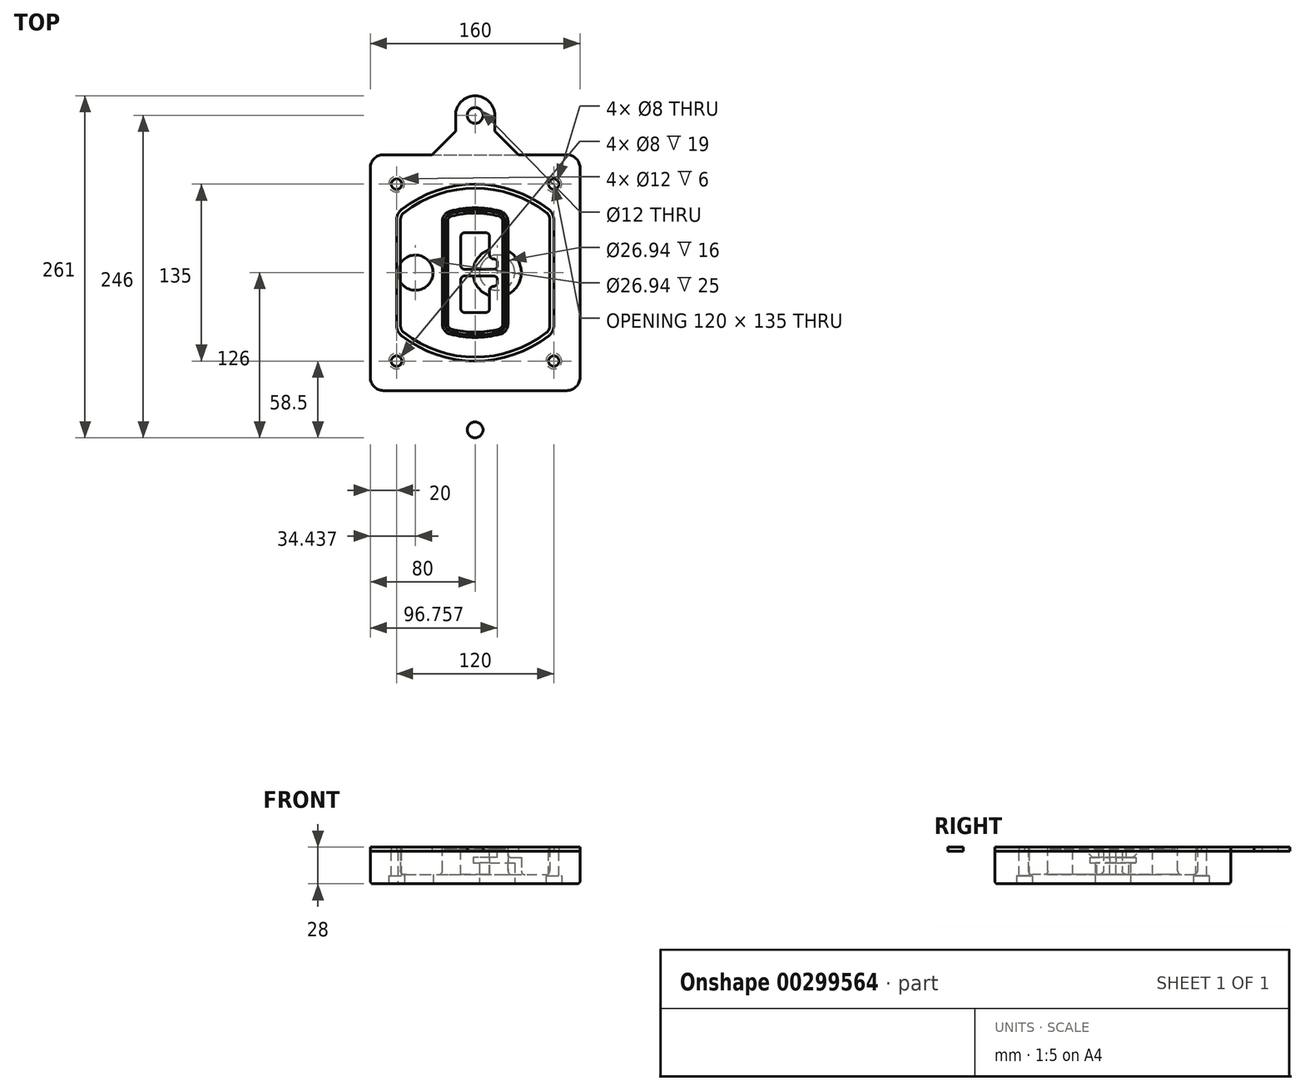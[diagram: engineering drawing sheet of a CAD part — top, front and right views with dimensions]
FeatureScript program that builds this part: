
annotation { "Feature Type Name" : "Feature", "Feature Type Description" : "" }
export const myFeature = defineFeature(function(context is Context, id is Id, definition is map)
    precondition{}
    {
        {
            var Q0;
            Q0=qCreatedBy(makeId("Top.planeOp"),FACE);
            var sketch = newSketch(context, id + "F0", { "sketchPlane" : qUnion([Q0])});
            skPoint(sketch, "E0.rect.middle", {"position": v(0, 0) * mm});
            skLineSegment(sketch, "E1.bottom", {"start": v(-70, -90) * mm, "end": v(70, -90) * mm});
            skLineSegment(sketch, "E1.top", {"start": v(-70, 90) * mm, "end": v(70, 90) * mm});
            skLineSegment(sketch, "E1.left", {"start": v(-80, -80) * mm, "end": v(-80, 80) * mm});
            skLineSegment(sketch, "E1.right", {"start": v(80, -80) * mm, "end": v(80, 80) * mm});
            skLineSegment(sketch, "E2", {"start": v(-80, 90) * mm, "end": v(80, -90) * mm, "construction": true});
            skLineSegment(sketch, "E3", {"start": v(80, 90) * mm, "end": v(-80, -90) * mm, "construction": true});
            skCircle(sketch, "E4", {"center": v(-60, 67.5) * mm, "radius": 4 * mm});
            skCircle(sketch, "E5", {"center": v(60, 67.5) * mm, "radius": 4 * mm});
            skCircle(sketch, "E6", {"center": v(60, -67.5) * mm, "radius": 4 * mm});
            skCircle(sketch, "E7", {"center": v(-60, -67.5) * mm, "radius": 4 * mm});
            skLineSegment(sketch, "E8", {"start": v(-60, 67.5) * mm, "end": v(60, 67.5) * mm, "construction": true});
            skLineSegment(sketch, "E9", {"start": v(60, 67.5) * mm, "end": v(60, -67.5) * mm, "construction": true});
            skLineSegment(sketch, "E10", {"start": v(60, -67.5) * mm, "end": v(-60, -67.5) * mm, "construction": true});
            skLineSegment(sketch, "E11", {"start": v(-60, -67.5) * mm, "end": v(-60, 67.5) * mm, "construction": true});
            skLineSegment(sketch, "E12", {"start": v(-60, 40.3) * mm, "end": v(-60, -40.3) * mm});
            skLineSegment(sketch, "E13", {"start": v(60, 40.3) * mm, "end": v(60, -40.3) * mm});
            skArc(sketch, "E14", {"start": v(56.15, 48.18) * mm, "mid": v(0, 67.5) * mm, "end": v(-56.15, 48.18) * mm});
            skArc(sketch, "E15", {"start": v(-56.15, -48.18) * mm, "mid": v(0, -67.5) * mm, "end": v(56.15, -48.18) * mm});
            skLineSegment(sketch, "E16", {"start": v(-60, 0) * mm, "end": v(60, 0) * mm, "construction": true});
            skPoint(sketch, "E17.visualSharp", {"position": v(-60, -45) * mm});
            skArc(sketch, "E17.filletArc", {"start": v(-60, -40.3) * mm, "mid": v(-58.99, -44.68) * mm, "end": v(-56.15, -48.18) * mm});
            skPoint(sketch, "E18.visualSharp", {"position": v(-60, 45) * mm});
            skArc(sketch, "E18.filletArc", {"start": v(-56.15, 48.18) * mm, "mid": v(-58.99, 44.68) * mm, "end": v(-60, 40.3) * mm});
            skPoint(sketch, "E19.visualSharp", {"position": v(60, 45) * mm});
            skArc(sketch, "E19.filletArc", {"start": v(60, 40.3) * mm, "mid": v(58.99, 44.68) * mm, "end": v(56.15, 48.18) * mm});
            skPoint(sketch, "E20.visualSharp", {"position": v(60, -45) * mm});
            skArc(sketch, "E20.filletArc", {"start": v(56.15, -48.18) * mm, "mid": v(58.99, -44.68) * mm, "end": v(60, -40.3) * mm});
            skPoint(sketch, "E21.visualSharp", {"position": v(-80, 90) * mm});
            skArc(sketch, "E21.filletArc", {"start": v(-70, 90) * mm, "mid": v(-77.07, 87.07) * mm, "end": v(-80, 80) * mm});
            skPoint(sketch, "E22.visualSharp", {"position": v(80, 90) * mm});
            skArc(sketch, "E22.filletArc", {"start": v(80, 80) * mm, "mid": v(77.07, 87.07) * mm, "end": v(70, 90) * mm});
            skPoint(sketch, "E23.visualSharp", {"position": v(80, -90) * mm});
            skArc(sketch, "E23.filletArc", {"start": v(70, -90) * mm, "mid": v(77.07, -87.07) * mm, "end": v(80, -80) * mm});
            skPoint(sketch, "E24.visualSharp", {"position": v(-80, -90) * mm});
            skArc(sketch, "E24.filletArc", {"start": v(-80, -80) * mm, "mid": v(-77.07, -87.07) * mm, "end": v(-70, -90) * mm});
            skArc(sketch, "E25.0", {"start": v(57, 40.3) * mm, "mid": v(56.3, 43.36) * mm, "end": v(54.3, 45.81) * mm});
            skLineSegment(sketch, "E25.1", {"start": v(57, 40.3) * mm, "end": v(57, -40.3) * mm});
            skArc(sketch, "E25.2", {"start": v(54.3, -45.81) * mm, "mid": v(56.3, -43.36) * mm, "end": v(57, -40.3) * mm});
            skArc(sketch, "E25.3", {"start": v(-54.3, -45.81) * mm, "mid": v(0, -64.5) * mm, "end": v(54.3, -45.81) * mm});
            skArc(sketch, "E25.4", {"start": v(-57, -40.3) * mm, "mid": v(-56.3, -43.36) * mm, "end": v(-54.3, -45.81) * mm});
            skArc(sketch, "E25.5", {"start": v(54.3, 45.81) * mm, "mid": v(0, 64.5) * mm, "end": v(-54.3, 45.81) * mm});
            skLineSegment(sketch, "E25.6", {"start": v(-57, 40.3) * mm, "end": v(-57, -40.3) * mm});
            skArc(sketch, "E25.7", {"start": v(-54.3, 45.81) * mm, "mid": v(-56.3, 43.36) * mm, "end": v(-57, 40.3) * mm});
            skArc(sketch, "E26.0", {"start": v(-58.62, 51.33) * mm, "mid": v(-62.58, 46.43) * mm, "end": v(-64, 40.3) * mm});
            skArc(sketch, "E26.1", {"start": v(58.62, 51.33) * mm, "mid": v(0, 71.5) * mm, "end": v(-58.62, 51.33) * mm});
            skArc(sketch, "E26.2", {"start": v(64, 40.3) * mm, "mid": v(62.58, 46.43) * mm, "end": v(58.62, 51.33) * mm});
            skLineSegment(sketch, "E26.3", {"start": v(64, 40.3) * mm, "end": v(64, -40.3) * mm});
            skArc(sketch, "E26.4", {"start": v(58.62, -51.33) * mm, "mid": v(62.58, -46.43) * mm, "end": v(64, -40.3) * mm});
            skLineSegment(sketch, "E26.5", {"start": v(-64, 40.3) * mm, "end": v(-64, -40.3) * mm});
            skArc(sketch, "E26.6", {"start": v(-58.62, -51.33) * mm, "mid": v(0, -71.5) * mm, "end": v(58.62, -51.33) * mm});
            skArc(sketch, "E26.7", {"start": v(-64, -40.3) * mm, "mid": v(-62.58, -46.43) * mm, "end": v(-58.62, -51.33) * mm});
            skSolve(sketch);
        }
        {
            var Q0;
            Q0=makeQuery(id+"F0.imprint","IMPRINT",FACE,{"disambiguationData":[TD([[makeQuery(id+"F0.imprint","IMPRINT",EDGE,{"derivedFrom":sQuery(id+"F0.wireOp",EDGE,"E1.bottom")}),1.0]])]});
            var Q1;
            Q1=makeQuery(id+"F0.imprint","IMPRINT",FACE,{"disambiguationData":[TD([[makeQuery(id+"F0.imprint","IMPRINT",EDGE,{"derivedFrom":sQuery(id+"F0.wireOp",EDGE,"E12")}),1.0]])]});
            var Q2;
            Q2=makeQuery(id+"F0.imprint","IMPRINT",FACE,{"disambiguationData":[TD([[makeQuery(id+"F0.imprint","IMPRINT",EDGE,{"derivedFrom":sQuery(id+"F0.wireOp",EDGE,"E25.0")}),1.0]])]});
            var Q3;
            Q3=makeQuery(id+"F0.imprint","IMPRINT",FACE,{"disambiguationData":[TD([[makeQuery(id+"F0.imprint","IMPRINT",EDGE,{"derivedFrom":sQuery(id+"F0.wireOp",EDGE,"E12")}),-1.0]])]});
            extrude(context, id + "F1", {"entities" : qUnion([Q0, Q1, Q2, Q3]), "oppositeDirection" : true, "depth" : 25 * mm});
        }
        {
            var Q0;
            Q0=makeQuery(id+"F0.imprint","IMPRINT",FACE,{"disambiguationData":[TD([[makeQuery(id+"F0.imprint","IMPRINT",EDGE,{"derivedFrom":sQuery(id+"F0.wireOp",EDGE,"E12")}),1.0]])]});
            extrude(context, id + "F2", {"entities" : qUnion([Q0]), "operationType" : NewBodyOperationType.ADD, "depth" : 3 * mm});
        }
        {
            var Q0;
            Q0=makeQuery(id+"F0.imprint","IMPRINT",FACE,{"disambiguationData":[TD([[makeQuery(id+"F0.imprint","IMPRINT",EDGE,{"derivedFrom":sQuery(id+"F0.wireOp",EDGE,"E25.0")}),1.0]])]});
            extrude(context, id + "F3", {"entities" : qUnion([Q0]), "operationType" : NewBodyOperationType.REMOVE, "oppositeDirection" : true, "depth" : 18 * mm});
        }
        {
            var Q0;
            Q0=makeQuery(id+"F2.opExtrude","CAP_FACE",FACE,{"disambiguationData":[OSD([sQuery(id+"F0.wireOp",EDGE,"E12"),sQuery(id+"F0.wireOp",EDGE,"E13"),sQuery(id+"F0.wireOp",EDGE,"E14"),sQuery(id+"F0.wireOp",EDGE,"E15"),sQuery(id+"F0.wireOp",EDGE,"E17.filletArc"),sQuery(id+"F0.wireOp",EDGE,"E18.filletArc"),sQuery(id+"F0.wireOp",EDGE,"E19.filletArc"),sQuery(id+"F0.wireOp",EDGE,"E20.filletArc"),sQuery(id+"F0.wireOp",EDGE,"E25.0"),sQuery(id+"F0.wireOp",EDGE,"E25.1"),sQuery(id+"F0.wireOp",EDGE,"E25.2"),sQuery(id+"F0.wireOp",EDGE,"E25.3"),sQuery(id+"F0.wireOp",EDGE,"E25.4"),sQuery(id+"F0.wireOp",EDGE,"E25.5"),sQuery(id+"F0.wireOp",EDGE,"E25.6"),sQuery(id+"F0.wireOp",EDGE,"E25.7")])],"isStart":false});
            var sketch = newSketch(context, id + "F4", { "sketchPlane" : qUnion([Q0])});
            skArc(sketch, "E27.0", {"start": v(-19.08, -46.97) * mm, "mid": v(0, -49.5) * mm, "end": v(19.08, -46.97) * mm});
            skArc(sketch, "E28.0", {"start": v(19.08, 46.97) * mm, "mid": v(0, 49.5) * mm, "end": v(-19.08, 46.97) * mm});
            skLineSegment(sketch, "E29", {"start": v(-25, 39.25) * mm, "end": v(-25, -39.25) * mm});
            skLineSegment(sketch, "E30", {"start": v(25, 39.25) * mm, "end": v(25, -39.25) * mm});
            skLineSegment(sketch, "E31", {"start": v(-25, 45.1) * mm, "end": v(25, 45.1) * mm, "construction": true});
            skLineSegment(sketch, "E32", {"start": v(-25, -45.1) * mm, "end": v(25, -45.1) * mm, "construction": true});
            skPoint(sketch, "E33.visualSharp", {"position": v(-25, 45.1) * mm});
            skArc(sketch, "E33.filletArc", {"start": v(-19.08, 46.97) * mm, "mid": v(-23.35, 44.11) * mm, "end": v(-25, 39.25) * mm});
            skPoint(sketch, "E34.visualSharp", {"position": v(25, 45.1) * mm});
            skArc(sketch, "E34.filletArc", {"start": v(25, 39.25) * mm, "mid": v(23.35, 44.11) * mm, "end": v(19.08, 46.97) * mm});
            skPoint(sketch, "E35.visualSharp", {"position": v(25, -45.1) * mm});
            skArc(sketch, "E35.filletArc", {"start": v(19.08, -46.97) * mm, "mid": v(23.35, -44.11) * mm, "end": v(25, -39.25) * mm});
            skPoint(sketch, "E36.visualSharp", {"position": v(-25, -45.1) * mm});
            skArc(sketch, "E36.filletArc", {"start": v(-25, -39.25) * mm, "mid": v(-23.35, -44.11) * mm, "end": v(-19.08, -46.97) * mm});
            skArc(sketch, "E37.0", {"start": v(54.3, 45.81) * mm, "mid": v(0, 64.5) * mm, "end": v(-54.3, 45.81) * mm});
            skArc(sketch, "E37.1", {"start": v(-54.3, 45.81) * mm, "mid": v(-56.3, 43.36) * mm, "end": v(-57, 40.3) * mm});
            skLineSegment(sketch, "E37.2", {"start": v(-57, 40.3) * mm, "end": v(-57, -40.3) * mm});
            skArc(sketch, "E37.3", {"start": v(-57, -40.3) * mm, "mid": v(-56.3, -43.36) * mm, "end": v(-54.3, -45.81) * mm});
            skArc(sketch, "E37.4", {"start": v(-54.3, -45.81) * mm, "mid": v(0, -64.5) * mm, "end": v(54.3, -45.81) * mm});
            skArc(sketch, "E37.5", {"start": v(54.3, -45.81) * mm, "mid": v(56.3, -43.36) * mm, "end": v(57, -40.3) * mm});
            skLineSegment(sketch, "E37.6", {"start": v(57, 40.3) * mm, "end": v(57, -40.3) * mm});
            skArc(sketch, "E37.7", {"start": v(57, 40.3) * mm, "mid": v(56.3, 43.36) * mm, "end": v(54.3, 45.81) * mm});
            skLineSegment(sketch, "E38.0", {"start": v(23, 39.25) * mm, "end": v(23, -39.25) * mm});
            skArc(sketch, "E38.1", {"start": v(18.56, -45.04) * mm, "mid": v(21.76, -42.9) * mm, "end": v(23, -39.25) * mm});
            skArc(sketch, "E38.2", {"start": v(-18.56, -45.04) * mm, "mid": v(0, -47.5) * mm, "end": v(18.56, -45.04) * mm});
            skArc(sketch, "E38.3", {"start": v(-23, -39.25) * mm, "mid": v(-21.76, -42.9) * mm, "end": v(-18.56, -45.04) * mm});
            skLineSegment(sketch, "E38.4", {"start": v(-23, 39.25) * mm, "end": v(-23, -39.25) * mm});
            skArc(sketch, "E38.5", {"start": v(23, 39.25) * mm, "mid": v(21.76, 42.9) * mm, "end": v(18.56, 45.04) * mm});
            skArc(sketch, "E38.6", {"start": v(-18.56, 45.04) * mm, "mid": v(-21.76, 42.9) * mm, "end": v(-23, 39.25) * mm});
            skArc(sketch, "E38.7", {"start": v(18.56, 45.04) * mm, "mid": v(0, 47.5) * mm, "end": v(-18.56, 45.04) * mm});
            skArc(sketch, "E39.0", {"start": v(21, 39.25) * mm, "mid": v(20.18, 41.68) * mm, "end": v(18.04, 43.1) * mm});
            skLineSegment(sketch, "E39.1", {"start": v(21, 39.25) * mm, "end": v(21, -39.25) * mm});
            skArc(sketch, "E39.2", {"start": v(18.04, -43.1) * mm, "mid": v(20.18, -41.68) * mm, "end": v(21, -39.25) * mm});
            skArc(sketch, "E39.3", {"start": v(-18.04, -43.1) * mm, "mid": v(0, -45.5) * mm, "end": v(18.04, -43.1) * mm});
            skArc(sketch, "E39.4", {"start": v(-21, -39.25) * mm, "mid": v(-20.18, -41.68) * mm, "end": v(-18.04, -43.1) * mm});
            skArc(sketch, "E39.5", {"start": v(18.04, 43.1) * mm, "mid": v(0, 45.5) * mm, "end": v(-18.04, 43.1) * mm});
            skLineSegment(sketch, "E39.6", {"start": v(-21, 39.25) * mm, "end": v(-21, -39.25) * mm});
            skArc(sketch, "E39.7", {"start": v(-18.04, 43.1) * mm, "mid": v(-20.18, 41.68) * mm, "end": v(-21, 39.25) * mm});
            skLineSegment(sketch, "E40", {"start": v(-25, 0) * mm, "end": v(25, 0) * mm, "construction": true});
            skLineSegment(sketch, "E41", {"start": v(-11, 5.5) * mm, "end": v(-11, 27.5) * mm});
            skLineSegment(sketch, "E42", {"start": v(-8, 30.5) * mm, "end": v(8, 30.5) * mm});
            skLineSegment(sketch, "E43", {"start": v(11, 27.5) * mm, "end": v(11, 13.5) * mm});
            skLineSegment(sketch, "E44", {"start": v(14, 10.5) * mm, "end": v(14, 10.5) * mm});
            skLineSegment(sketch, "E45", {"start": v(17, 7.5) * mm, "end": v(17, 5.5) * mm});
            skLineSegment(sketch, "E46", {"start": v(14, 2.5) * mm, "end": v(-8, 2.5) * mm});
            skPoint(sketch, "E47.visualSharp", {"position": v(-11, 30.5) * mm});
            skArc(sketch, "E47.filletArc", {"start": v(-8, 30.5) * mm, "mid": v(-10.12, 29.62) * mm, "end": v(-11, 27.5) * mm});
            skPoint(sketch, "E48.visualSharp", {"position": v(11, 30.5) * mm});
            skArc(sketch, "E48.filletArc", {"start": v(11, 27.5) * mm, "mid": v(10.12, 29.62) * mm, "end": v(8, 30.5) * mm});
            skPoint(sketch, "E49.visualSharp", {"position": v(11, 10.5) * mm});
            skArc(sketch, "E49.filletArc", {"start": v(11, 13.5) * mm, "mid": v(11.88, 11.38) * mm, "end": v(14, 10.5) * mm});
            skPoint(sketch, "E50.visualSharp", {"position": v(17, 10.5) * mm});
            skArc(sketch, "E50.filletArc", {"start": v(17, 7.5) * mm, "mid": v(16.12, 9.62) * mm, "end": v(14, 10.5) * mm});
            skPoint(sketch, "E51.visualSharp", {"position": v(17, 2.5) * mm});
            skArc(sketch, "E51.filletArc", {"start": v(14, 2.5) * mm, "mid": v(16.12, 3.38) * mm, "end": v(17, 5.5) * mm});
            skPoint(sketch, "E52.visualSharp", {"position": v(-11, 2.5) * mm});
            skArc(sketch, "E52.filletArc", {"start": v(-11, 5.5) * mm, "mid": v(-10.12, 3.38) * mm, "end": v(-8, 2.5) * mm});
            skLineSegment(sketch, "E53.0.MirrorCS", {"start": v(14, -2.5) * mm, "end": v(-8, -2.5) * mm});
            skArc(sketch, "E54.0.MirrorCS", {"start": v(-11, -5.5) * mm, "mid": v(-10.12, -3.38) * mm, "end": v(-8, -2.5) * mm});
            skLineSegment(sketch, "E55.0.MirrorCS", {"start": v(-11, -5.5) * mm, "end": v(-11, -27.5) * mm});
            skArc(sketch, "E56.0.MirrorCS", {"start": v(-8, -30.5) * mm, "mid": v(-10.12, -29.62) * mm, "end": v(-11, -27.5) * mm});
            skLineSegment(sketch, "E57.0.MirrorCS", {"start": v(-8, -30.5) * mm, "end": v(8, -30.5) * mm});
            skArc(sketch, "E58.0.MirrorCS", {"start": v(11, -27.5) * mm, "mid": v(10.12, -29.62) * mm, "end": v(8, -30.5) * mm});
            skLineSegment(sketch, "E59.0.MirrorCS", {"start": v(11, -27.5) * mm, "end": v(11, -13.5) * mm});
            skArc(sketch, "E60.0.MirrorCS", {"start": v(11, -13.5) * mm, "mid": v(11.88, -11.38) * mm, "end": v(14, -10.5) * mm});
            skArc(sketch, "E61.0.MirrorCS", {"start": v(17, -7.5) * mm, "mid": v(16.12, -9.62) * mm, "end": v(14, -10.5) * mm});
            skLineSegment(sketch, "E62.0.MirrorCS", {"start": v(17, -7.5) * mm, "end": v(17, -5.5) * mm});
            skArc(sketch, "E63.0.MirrorCS", {"start": v(14, -2.5) * mm, "mid": v(16.12, -3.38) * mm, "end": v(17, -5.5) * mm});
            skSolve(sketch);
        }
        {
            var Q0;
            Q0=makeQuery(id+"F4.imprint","IMPRINT",FACE,{"disambiguationData":[TD([[makeQuery(id+"F4.imprint","IMPRINT",EDGE,{"derivedFrom":sQuery(id+"F4.wireOp",EDGE,"E27.0")}),1.0]])]});
            var Q1;
            Q1=makeQuery(id+"F4.imprint","IMPRINT",FACE,{"disambiguationData":[TD([[makeQuery(id+"F4.imprint","IMPRINT",EDGE,{"derivedFrom":sQuery(id+"F4.wireOp",EDGE,"E38.0")}),-1.0]])]});
            var Q2;
            Q2=makeQuery(id+"F4.imprint","IMPRINT",FACE,{"disambiguationData":[TD([[makeQuery(id+"F4.imprint","IMPRINT",EDGE,{"derivedFrom":sQuery(id+"F4.wireOp",EDGE,"E39.0")}),1.0]])]});
            extrude(context, id + "F5", {"entities" : qUnion([Q0, Q1, Q2]), "operationType" : NewBodyOperationType.ADD, "endBound" : BoundingType.UP_TO_NEXT, "oppositeDirection" : true, "depth" : 25 * mm});
        }
        {
            var Q0;
            Q0=makeQuery(id+"F4.imprint","IMPRINT",FACE,{"disambiguationData":[TD([[makeQuery(id+"F4.imprint","IMPRINT",EDGE,{"derivedFrom":sQuery(id+"F4.wireOp",EDGE,"E38.0")}),-1.0]])]});
            extrude(context, id + "F6", {"entities" : qUnion([Q0]), "operationType" : NewBodyOperationType.REMOVE, "oppositeDirection" : true, "depth" : 2 * mm});
        }
        {
            var Q0;
            Q0=makeQuery(id+"F1.opExtrude","CAP_FACE",FACE,{"disambiguationData":[OSD([sQuery(id+"F0.wireOp",EDGE,"E1.bottom"),sQuery(id+"F0.wireOp",EDGE,"E1.top"),sQuery(id+"F0.wireOp",EDGE,"E1.left"),sQuery(id+"F0.wireOp",EDGE,"E1.right"),sQuery(id+"F0.wireOp",EDGE,"E4"),sQuery(id+"F0.wireOp",EDGE,"E5"),sQuery(id+"F0.wireOp",EDGE,"E6"),sQuery(id+"F0.wireOp",EDGE,"E7"),sQuery(id+"F0.wireOp",EDGE,"E21.filletArc"),sQuery(id+"F0.wireOp",EDGE,"E22.filletArc"),sQuery(id+"F0.wireOp",EDGE,"E23.filletArc"),sQuery(id+"F0.wireOp",EDGE,"E24.filletArc")])],"isStart":false});
            var sketch = newSketch(context, id + "F7", { "sketchPlane" : qUnion([Q0])});
            skCircle(sketch, "E64", {"center": v(16.76, 0) * mm, "radius": 13.47 * mm});
            skCircle(sketch, "E65", {"center": v(-45.56, 0) * mm, "radius": 13.47 * mm});
            skLineSegment(sketch, "E66", {"start": v(80, 0) * mm, "end": v(-80, 0) * mm});
            skCircle(sketch, "E67", {"center": v(16.76, 0) * mm, "radius": 18.47 * mm});
            skCircle(sketch, "E68", {"center": v(60, -67.5) * mm, "radius": 6 * mm});
            skCircle(sketch, "E69", {"center": v(-60, -67.5) * mm, "radius": 6 * mm});
            skCircle(sketch, "E70", {"center": v(-60, 67.5) * mm, "radius": 6 * mm});
            skCircle(sketch, "E71", {"center": v(60, 67.5) * mm, "radius": 6 * mm});
            skSolve(sketch);
        }
        {
            var Q0;
            {var subQ1=sQuery(id+"F7.wireOp",EDGE,"E66");var subQ4=sQuery(id+"F7.wireOp",EDGE,"E64");var subQ6=makeQuery(id+"F7.imprint","INTERSECT",VERTEX,{"disambiguationData":[OD(0.0)],"derivedFrom":[subQ4,subQ1]});Q0=makeQuery(id+"F7.imprint","IMPRINT",FACE,{"disambiguationData":[TD([[makeQuery(id+"F7.imprint","IMPRINT",EDGE,{"disambiguationData":[TD([[subQ6,-1.0]])],"derivedFrom":subQ4}),-1.0]])]});}
            var Q1;
            {var subQ0=sQuery(id+"F7.wireOp",EDGE,"E66");var subQ1=sQuery(id+"F7.wireOp",EDGE,"E64");var subQ3=makeQuery(id+"F7.imprint","INTERSECT",VERTEX,{"disambiguationData":[OD(0.0)],"derivedFrom":[subQ1,subQ0]});Q1=makeQuery(id+"F7.imprint","IMPRINT",FACE,{"disambiguationData":[TD([[makeQuery(id+"F7.imprint","IMPRINT",EDGE,{"disambiguationData":[TD([[subQ3,-1.0]])],"derivedFrom":subQ1}),1.0]])]});}
            var Q2;
            {var subQ0=sQuery(id+"F7.wireOp",EDGE,"E66");var subQ1=sQuery(id+"F7.wireOp",EDGE,"E64");var subQ3=makeQuery(id+"F7.imprint","INTERSECT",VERTEX,{"disambiguationData":[OD(0.0)],"derivedFrom":[subQ1,subQ0]});Q2=makeQuery(id+"F7.imprint","IMPRINT",FACE,{"disambiguationData":[TD([[makeQuery(id+"F7.imprint","IMPRINT",EDGE,{"disambiguationData":[TD([[subQ3,1.0]])],"derivedFrom":subQ1}),1.0]])]});}
            var Q3;
            {var subQ1=sQuery(id+"F7.wireOp",EDGE,"E66");var subQ4=sQuery(id+"F7.wireOp",EDGE,"E64");var subQ6=makeQuery(id+"F7.imprint","INTERSECT",VERTEX,{"disambiguationData":[OD(0.0)],"derivedFrom":[subQ4,subQ1]});Q3=makeQuery(id+"F7.imprint","IMPRINT",FACE,{"disambiguationData":[TD([[makeQuery(id+"F7.imprint","IMPRINT",EDGE,{"disambiguationData":[TD([[subQ6,1.0]])],"derivedFrom":subQ4}),-1.0]])]});}
            extrude(context, id + "F8", {"entities" : qUnion([Q0, Q1, Q2, Q3]), "operationType" : NewBodyOperationType.ADD, "oppositeDirection" : true, "depth" : 20 * mm});
        }
        {
            var Q0;
            {var subQ0=sQuery(id+"F7.wireOp",EDGE,"E66");var subQ1=sQuery(id+"F7.wireOp",EDGE,"E64");var subQ3=makeQuery(id+"F7.imprint","INTERSECT",VERTEX,{"disambiguationData":[OD(0.0)],"derivedFrom":[subQ1,subQ0]});Q0=makeQuery(id+"F7.imprint","IMPRINT",FACE,{"disambiguationData":[TD([[makeQuery(id+"F7.imprint","IMPRINT",EDGE,{"disambiguationData":[TD([[subQ3,-1.0]])],"derivedFrom":subQ1}),1.0]])]});}
            var Q1;
            {var subQ0=sQuery(id+"F7.wireOp",EDGE,"E66");var subQ1=sQuery(id+"F7.wireOp",EDGE,"E64");var subQ3=makeQuery(id+"F7.imprint","INTERSECT",VERTEX,{"disambiguationData":[OD(0.0)],"derivedFrom":[subQ1,subQ0]});Q1=makeQuery(id+"F7.imprint","IMPRINT",FACE,{"disambiguationData":[TD([[makeQuery(id+"F7.imprint","IMPRINT",EDGE,{"disambiguationData":[TD([[subQ3,1.0]])],"derivedFrom":subQ1}),1.0]])]});}
            extrude(context, id + "F9", {"entities" : qUnion([Q0, Q1]), "operationType" : NewBodyOperationType.REMOVE, "oppositeDirection" : true, "depth" : 16 * mm});
        }
        {
            var Q0;
            {var subQ0=sQuery(id+"F7.wireOp",EDGE,"E66");var subQ1=sQuery(id+"F7.wireOp",EDGE,"E65");var subQ3=makeQuery(id+"F7.imprint","INTERSECT",VERTEX,{"disambiguationData":[OD(0.0)],"derivedFrom":[subQ1,subQ0]});Q0=makeQuery(id+"F7.imprint","IMPRINT",FACE,{"disambiguationData":[TD([[makeQuery(id+"F7.imprint","IMPRINT",EDGE,{"disambiguationData":[TD([[subQ3,-1.0]])],"derivedFrom":subQ1}),1.0]])]});}
            var Q1;
            {var subQ0=sQuery(id+"F7.wireOp",EDGE,"E66");var subQ1=sQuery(id+"F7.wireOp",EDGE,"E65");var subQ3=makeQuery(id+"F7.imprint","INTERSECT",VERTEX,{"disambiguationData":[OD(0.0)],"derivedFrom":[subQ1,subQ0]});Q1=makeQuery(id+"F7.imprint","IMPRINT",FACE,{"disambiguationData":[TD([[makeQuery(id+"F7.imprint","IMPRINT",EDGE,{"disambiguationData":[TD([[subQ3,1.0]])],"derivedFrom":subQ1}),1.0]])]});}
            extrude(context, id + "F10", {"entities" : qUnion([Q0, Q1]), "operationType" : NewBodyOperationType.REMOVE, "oppositeDirection" : true, "depth" : 25 * mm});
        }
        {
            var Q0;
            Q0=makeQuery(id+"F7.imprint","IMPRINT",FACE,{"disambiguationData":[TD([[makeQuery(id+"F7.imprint","IMPRINT",EDGE,{"derivedFrom":sQuery(id+"F7.wireOp",EDGE,"E68")}),1.0]])]});
            var Q1;
            Q1=makeQuery(id+"F7.imprint","IMPRINT",FACE,{"disambiguationData":[TD([[makeQuery(id+"F7.imprint","IMPRINT",EDGE,{"derivedFrom":makeQuery(id+"F1.opExtrude","CAP_EDGE",EDGE,{"disambiguationData":[OSD([sQuery(id+"F0.wireOp",EDGE,"E5")])],"isStart":false})}),-1.0]])]});
            var Q2;
            Q2=makeQuery(id+"F7.imprint","IMPRINT",FACE,{"disambiguationData":[TD([[makeQuery(id+"F7.imprint","IMPRINT",EDGE,{"derivedFrom":sQuery(id+"F7.wireOp",EDGE,"E69")}),1.0]])]});
            var Q3;
            Q3=makeQuery(id+"F7.imprint","IMPRINT",FACE,{"disambiguationData":[TD([[makeQuery(id+"F7.imprint","IMPRINT",EDGE,{"derivedFrom":makeQuery(id+"F1.opExtrude","CAP_EDGE",EDGE,{"disambiguationData":[OSD([sQuery(id+"F0.wireOp",EDGE,"E4")])],"isStart":false})}),-1.0]])]});
            var Q4;
            Q4=makeQuery(id+"F7.imprint","IMPRINT",FACE,{"disambiguationData":[TD([[makeQuery(id+"F7.imprint","IMPRINT",EDGE,{"derivedFrom":sQuery(id+"F7.wireOp",EDGE,"E70")}),1.0]])]});
            var Q5;
            Q5=makeQuery(id+"F7.imprint","IMPRINT",FACE,{"disambiguationData":[TD([[makeQuery(id+"F7.imprint","IMPRINT",EDGE,{"derivedFrom":makeQuery(id+"F1.opExtrude","CAP_EDGE",EDGE,{"disambiguationData":[OSD([sQuery(id+"F0.wireOp",EDGE,"E7")])],"isStart":false})}),-1.0]])]});
            var Q6;
            Q6=makeQuery(id+"F7.imprint","IMPRINT",FACE,{"disambiguationData":[TD([[makeQuery(id+"F7.imprint","IMPRINT",EDGE,{"derivedFrom":sQuery(id+"F7.wireOp",EDGE,"E71")}),1.0]])]});
            var Q7;
            Q7=makeQuery(id+"F7.imprint","IMPRINT",FACE,{"disambiguationData":[TD([[makeQuery(id+"F7.imprint","IMPRINT",EDGE,{"derivedFrom":makeQuery(id+"F1.opExtrude","CAP_EDGE",EDGE,{"disambiguationData":[OSD([sQuery(id+"F0.wireOp",EDGE,"E6")])],"isStart":false})}),-1.0]])]});
            extrude(context, id + "F11", {"entities" : qUnion([Q0, Q1, Q2, Q3, Q4, Q5, Q6, Q7]), "operationType" : NewBodyOperationType.REMOVE, "oppositeDirection" : true, "depth" : 6 * mm});
        }
        {
            var Q0;
            Q0=makeQuery(id+"F9.boolean.opBoolean","COPY",FACE,{"derivedFrom":makeQuery(id+"F9.opExtrude","CAP_FACE",FACE,{"disambiguationData":[OSD([sQuery(id+"F7.wireOp",EDGE,"E64")])],"isStart":false})});
            var sketch = newSketch(context, id + "F12", { "sketchPlane" : qUnion([Q0])});
            skArc(sketch, "E72.0", {"start": v(11, 17.55) * mm, "mid": v(2.57, 11.82) * mm, "end": v(-1.54, 2.5) * mm});
            skArc(sketch, "E72.1", {"start": v(-1.54, -2.5) * mm, "mid": v(2.57, -11.82) * mm, "end": v(11, -17.55) * mm});
            skLineSegment(sketch, "E73", {"start": v(-1.54, -2.5) * mm, "end": v(14, -2.5) * mm});
            skLineSegment(sketch, "E74.0", {"start": v(14, 2.5) * mm, "end": v(-1.54, 2.5) * mm});
            skArc(sketch, "E74.1", {"start": v(14, 2.5) * mm, "mid": v(16.12, 3.38) * mm, "end": v(17, 5.5) * mm});
            skLineSegment(sketch, "E74.2", {"start": v(17, 7.5) * mm, "end": v(17, 5.5) * mm});
            skArc(sketch, "E74.3", {"start": v(17, 7.5) * mm, "mid": v(16.12, 9.62) * mm, "end": v(14, 10.5) * mm});
            skArc(sketch, "E74.4", {"start": v(11, 13.5) * mm, "mid": v(11.88, 11.38) * mm, "end": v(14, 10.5) * mm});
            skLineSegment(sketch, "E74.5", {"start": v(11, 17.55) * mm, "end": v(11, 13.5) * mm});
            skLineSegment(sketch, "E74.7", {"start": v(14, -2.5) * mm, "end": v(-1.54, -2.5) * mm});
            skArc(sketch, "E74.8", {"start": v(14, -2.5) * mm, "mid": v(16.12, -3.38) * mm, "end": v(17, -5.5) * mm});
            skLineSegment(sketch, "E74.9", {"start": v(17, -7.5) * mm, "end": v(17, -5.5) * mm});
            skArc(sketch, "E74.10", {"start": v(17, -7.5) * mm, "mid": v(16.12, -9.62) * mm, "end": v(14, -10.5) * mm});
            skArc(sketch, "E74.11", {"start": v(11, -13.5) * mm, "mid": v(11.88, -11.38) * mm, "end": v(14, -10.5) * mm});
            skLineSegment(sketch, "E74.12", {"start": v(11, -17.55) * mm, "end": v(11, -13.5) * mm});
            skPoint(sketch, "E75.orphan", {"position": v(11, -27.5) * mm});
            skPoint(sketch, "E76.orphan", {"position": v(-8, -2.5) * mm});
            skPoint(sketch, "E77.orphan", {"position": v(-8, 2.5) * mm});
            skPoint(sketch, "E78.orphan", {"position": v(11, 27.5) * mm});
            skSolve(sketch);
        }
        {
            var Q0;
            {var subQ7=sQuery(id+"F12.wireOp",EDGE,"E72.0");var subQ14=sQuery(id+"F12.wireOp",EDGE,"E72.1");var subQ16=sQuery(id+"F12.wireOp",EDGE,"E74.1");var subQ18=sQuery(id+"F12.wireOp",EDGE,"E74.8");Q0=qUnion([makeQuery(id+"F12.imprint","IMPRINT",FACE,{"disambiguationData":[TD([[makeQuery(id+"F12.imprint","IMPRINT",EDGE,{"derivedFrom":subQ7}),1.0]])]}),makeQuery(id+"F12.imprint","IMPRINT",FACE,{"disambiguationData":[TD([[makeQuery(id+"F12.imprint","IMPRINT",EDGE,{"derivedFrom":subQ14}),1.0]])]}),makeQuery(id+"F12.imprint","IMPRINT",FACE,{"disambiguationData":[TD([[makeQuery(id+"F12.imprint","IMPRINT",EDGE,{"derivedFrom":subQ16}),1.0]])]}),makeQuery(id+"F12.imprint","IMPRINT",FACE,{"disambiguationData":[TD([[makeQuery(id+"F12.imprint","IMPRINT",EDGE,{"derivedFrom":subQ18}),-1.0]])]})]);}
            var Q1;
            Q1=makeQuery(id+"F5.boolean.opBoolean","SPLIT",FACE,{"disambiguationData":[TD([makeQuery(id+"F5.opExtrude","SWEPT_FACE",FACE,{"disambiguationData":[OSD([sQuery(id+"F4.wireOp",EDGE,"E41")])]})])],"derivedFrom":makeQuery(id+"F3.boolean.opBoolean","COPY",FACE,{"derivedFrom":makeQuery(id+"F3.opExtrude","CAP_FACE",FACE,{"disambiguationData":[OSD([sQuery(id+"F0.wireOp",EDGE,"E25.0"),sQuery(id+"F0.wireOp",EDGE,"E25.1"),sQuery(id+"F0.wireOp",EDGE,"E25.2"),sQuery(id+"F0.wireOp",EDGE,"E25.3"),sQuery(id+"F0.wireOp",EDGE,"E25.4"),sQuery(id+"F0.wireOp",EDGE,"E25.5"),sQuery(id+"F0.wireOp",EDGE,"E25.6"),sQuery(id+"F0.wireOp",EDGE,"E25.7")])],"isStart":false})})});
            extrude(context, id + "F13", {"entities" : qUnion([Q0]), "operationType" : NewBodyOperationType.REMOVE, "endBound" : BoundingType.UP_TO_SURFACE, "endBoundEntityFace" : qUnion([Q1]), "depth" : 25 * mm});
        }
        {
            var Q0;
            Q0=makeQuery(id+"F3.boolean.opBoolean","COPY",EDGE,{"derivedFrom":makeQuery(id+"F3.opExtrude","CAP_EDGE",EDGE,{"disambiguationData":[OSD([sQuery(id+"F0.wireOp",EDGE,"E25.6")])],"isStart":false})});
            var Q1;
            Q1=makeQuery(id+"F8.boolean.opBoolean","INTERSECT",EDGE,{"derivedFrom":[makeQuery(id+"F5.opExtrude","SWEPT_FACE",FACE,{"disambiguationData":[OSD([sQuery(id+"F4.wireOp",EDGE,"E30")])]}),makeQuery(id+"F8.opExtrude","CAP_FACE",FACE,{"disambiguationData":[OSD([sQuery(id+"F7.wireOp",EDGE,"E67")])],"isStart":false})]});
            var Q2;
            Q2=makeQuery(id+"F8.boolean.opBoolean","INTERSECT",EDGE,{"disambiguationData":[OD(1.0)],"derivedFrom":[makeQuery(id+"F5.opExtrude","SWEPT_FACE",FACE,{"disambiguationData":[OSD([sQuery(id+"F4.wireOp",EDGE,"E30")])]}),makeQuery(id+"F8.opExtrude","SWEPT_FACE",FACE,{"disambiguationData":[OSD([sQuery(id+"F7.wireOp",EDGE,"E67")])]})]});
            var Q3;
            {var subQ0=sQuery(id+"F4.wireOp",EDGE,"E30");Q3=makeQuery(id+"F8.boolean.opBoolean","SPLIT",EDGE,{"disambiguationData":[TD([makeQuery(id+"F5.opExtrude","SWEPT_FACE",FACE,{"disambiguationData":[OSD([sQuery(id+"F4.wireOp",EDGE,"E35.filletArc")])]})])],"derivedFrom":makeQuery(id+"F5.opExtrude","CAP_EDGE",EDGE,{"disambiguationData":[OSD([subQ0])],"isStart":false})});}
            var Q4;
            {var subQ0=sQuery(id+"F0.wireOp",EDGE,"E25.7");var subQ1=sQuery(id+"F0.wireOp",EDGE,"E25.1");var subQ2=sQuery(id+"F0.wireOp",EDGE,"E25.6");var subQ3=sQuery(id+"F0.wireOp",EDGE,"E25.5");var subQ4=sQuery(id+"F0.wireOp",EDGE,"E25.4");var subQ5=sQuery(id+"F0.wireOp",EDGE,"E25.0");var subQ6=sQuery(id+"F0.wireOp",EDGE,"E25.2");var subQ7=sQuery(id+"F0.wireOp",EDGE,"E25.3");Q4=makeQuery(id+"F8.boolean.opBoolean","INTERSECT",EDGE,{"derivedFrom":[makeQuery(id+"F5.boolean.opBoolean","SPLIT",FACE,{"disambiguationData":[TD([makeQuery(id+"F2.opExtrude","SWEPT_FACE",FACE,{"disambiguationData":[OSD([subQ5])]})])],"derivedFrom":makeQuery(id+"F3.boolean.opBoolean","COPY",FACE,{"derivedFrom":makeQuery(id+"F3.opExtrude","CAP_FACE",FACE,{"disambiguationData":[OSD([subQ5,subQ1,subQ6,subQ7,subQ4,subQ3,subQ2,subQ0])],"isStart":false})})}),makeQuery(id+"F8.opExtrude","SWEPT_FACE",FACE,{"disambiguationData":[OSD([sQuery(id+"F7.wireOp",EDGE,"E67")])]})]});}
            var Q5;
            Q5=makeQuery(id+"F8.boolean.opBoolean","INTERSECT",EDGE,{"disambiguationData":[OD(0.0)],"derivedFrom":[makeQuery(id+"F5.opExtrude","SWEPT_FACE",FACE,{"disambiguationData":[OSD([sQuery(id+"F4.wireOp",EDGE,"E30")])]}),makeQuery(id+"F8.opExtrude","SWEPT_FACE",FACE,{"disambiguationData":[OSD([sQuery(id+"F7.wireOp",EDGE,"E67")])]})]});
            fillet(context, id + "F14", {"entities" : qUnion([Q0, Q1, Q2, Q3, Q4, Q5]), "radius" : 3 * mm, "tangentPropagation" : true, "allowEdgeOverflow" : false});
        }
        {
            var Q0;
            Q0=makeQuery(id+"F1.opExtrude","CAP_EDGE",EDGE,{"disambiguationData":[OSD([sQuery(id+"F0.wireOp",EDGE,"E1.bottom")])],"isStart":false});
            fillet(context, id + "F15", {"entities" : qUnion([Q0]), "radius" : 2 * mm, "tangentPropagation" : true, "allowEdgeOverflow" : false});
        }
        {
            var Q0;
            {var subQ0=sQuery(id+"F0.wireOp",EDGE,"E21.filletArc");var subQ1=sQuery(id+"F0.wireOp",EDGE,"E7");var subQ2=sQuery(id+"F0.wireOp",EDGE,"E6");var subQ3=sQuery(id+"F0.wireOp",EDGE,"E5");var subQ4=sQuery(id+"F0.wireOp",EDGE,"E4");var subQ5=sQuery(id+"F0.wireOp",EDGE,"E22.filletArc");var subQ6=sQuery(id+"F0.wireOp",EDGE,"E1.bottom");var subQ7=sQuery(id+"F0.wireOp",EDGE,"E1.right");var subQ8=sQuery(id+"F0.wireOp",EDGE,"E1.top");var subQ9=sQuery(id+"F0.wireOp",EDGE,"E1.left");var subQ10=sQuery(id+"F0.wireOp",EDGE,"E23.filletArc");var subQ11=sQuery(id+"F0.wireOp",EDGE,"E24.filletArc");Q0=makeQuery(id+"F2.boolean.opBoolean","SPLIT",FACE,{"disambiguationData":[TD([makeQuery(id+"F1.opExtrude","SWEPT_FACE",FACE,{"disambiguationData":[OSD([subQ6])]})])],"derivedFrom":makeQuery(id+"F1.opExtrude","CAP_FACE",FACE,{"disambiguationData":[OSD([subQ6,subQ8,subQ9,subQ7,subQ4,subQ3,subQ2,subQ1,subQ0,subQ5,subQ10,subQ11])],"isStart":true})});}
            var sketch = newSketch(context, id + "F16", { "sketchPlane" : qUnion([Q0])});
            skLineSegment(sketch, "E79", {"start": v(0, 90) * mm, "end": v(0, 120) * mm, "construction": true});
            skCircle(sketch, "E80", {"center": v(0, 120) * mm, "radius": 6 * mm});
            skArc(sketch, "E81", {"start": v(15, 120) * mm, "mid": v(0, 135) * mm, "end": v(-15, 120) * mm});
            skLineSegment(sketch, "E82", {"start": v(-15, 120) * mm, "end": v(-15, 108) * mm});
            skLineSegment(sketch, "E83", {"start": v(15, 120) * mm, "end": v(15, 108) * mm});
            skLineSegment(sketch, "E84", {"start": v(15, 108) * mm, "end": v(33, 90) * mm});
            skLineSegment(sketch, "E85", {"start": v(-15, 108) * mm, "end": v(-33, 90) * mm});
            skLineSegment(sketch, "E86", {"start": v(-80, 0) * mm, "end": v(80, 0) * mm, "construction": true});
            skLineSegment(sketch, "E87.MirrorCS", {"start": v(0, -90) * mm, "end": v(0, -120) * mm, "construction": true});
            skCircle(sketch, "E88.MirrorC", {"center": v(0, -120) * mm, "radius": 6 * mm});
            skArc(sketch, "E89.MirrorCS", {"start": v(15, -120) * mm, "mid": v(0, -135) * mm, "end": v(-15, -120) * mm});
            skLineSegment(sketch, "E90.MirrorCS", {"start": v(-15, -120) * mm, "end": v(-15, -108) * mm});
            skLineSegment(sketch, "E91.MirrorCS", {"start": v(15, -120) * mm, "end": v(15, -108) * mm});
            skLineSegment(sketch, "E92.MirrorCS", {"start": v(15, -108) * mm, "end": v(33, -90) * mm});
            skLineSegment(sketch, "E93.MirrorCS", {"start": v(-15, -108) * mm, "end": v(-33, -90) * mm});
            skSolve(sketch);
        }
        {
            var Q0;
            Q0=makeQuery(id+"F16.imprint","IMPRINT",FACE,{"disambiguationData":[TD([[makeQuery(id+"F16.imprint","IMPRINT",EDGE,{"derivedFrom":makeQuery(id+"F1.opExtrude","CAP_EDGE",EDGE,{"disambiguationData":[OSD([sQuery(id+"F0.wireOp",EDGE,"E1.left")])],"isStart":true})}),-1.0]])]});
            var Q1;
            Q1=makeQuery(id+"F16.imprint","IMPRINT",FACE,{"disambiguationData":[TD([[makeQuery(id+"F16.imprint","IMPRINT",EDGE,{"derivedFrom":sQuery(id+"F16.wireOp",EDGE,"E80")}),-1.0]])]});
            var Q2;
            Q2=makeQuery(id+"F16.imprint","IMPRINT",FACE,{"disambiguationData":[TD([[makeQuery(id+"F16.imprint","IMPRINT",EDGE,{"derivedFrom":sQuery(id+"F16.wireOp",EDGE,"E88.MirrorC")}),1.0]])]});
            var Q3;
            Q3=makeQuery(id+"F2.opExtrude","CAP_FACE",FACE,{"disambiguationData":[OSD([sQuery(id+"F0.wireOp",EDGE,"E12"),sQuery(id+"F0.wireOp",EDGE,"E13"),sQuery(id+"F0.wireOp",EDGE,"E14"),sQuery(id+"F0.wireOp",EDGE,"E15"),sQuery(id+"F0.wireOp",EDGE,"E17.filletArc"),sQuery(id+"F0.wireOp",EDGE,"E18.filletArc"),sQuery(id+"F0.wireOp",EDGE,"E19.filletArc"),sQuery(id+"F0.wireOp",EDGE,"E20.filletArc"),sQuery(id+"F0.wireOp",EDGE,"E25.0"),sQuery(id+"F0.wireOp",EDGE,"E25.1"),sQuery(id+"F0.wireOp",EDGE,"E25.2"),sQuery(id+"F0.wireOp",EDGE,"E25.3"),sQuery(id+"F0.wireOp",EDGE,"E25.4"),sQuery(id+"F0.wireOp",EDGE,"E25.5"),sQuery(id+"F0.wireOp",EDGE,"E25.6"),sQuery(id+"F0.wireOp",EDGE,"E25.7")])],"isStart":false});
            extrude(context, id + "F17", {"entities" : qUnion([Q0, Q1, Q2]), "endBound" : BoundingType.UP_TO_SURFACE, "endBoundEntityFace" : qUnion([Q3]), "depth" : 25 * mm});
        }
    });
